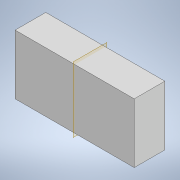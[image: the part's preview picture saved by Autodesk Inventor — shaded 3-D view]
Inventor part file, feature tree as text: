
AUTODESK INVENTOR PART (.ipt)
format: ipt  version: 2022 (Build 260153070, 153G)  size: 89,600 bytes
history: native  units: mm
features: extrude x1, plane x1, sketch x1
ambient origin geometry x8: Origin, YZ Plane, XZ Plane, XY Plane, X Axis, Y Axis, Z Axis, Center Point
bodies: Solid1 (feature_tree)
feature tree (3):
  extrude  "Extrusion1"  Depth=35.0mm
  plane  "Work Plane1"
  sketch  "Sketch1"  dims[d0=70.0mm d1=35.0mm d2=18.0mm d3=0.0mm]
